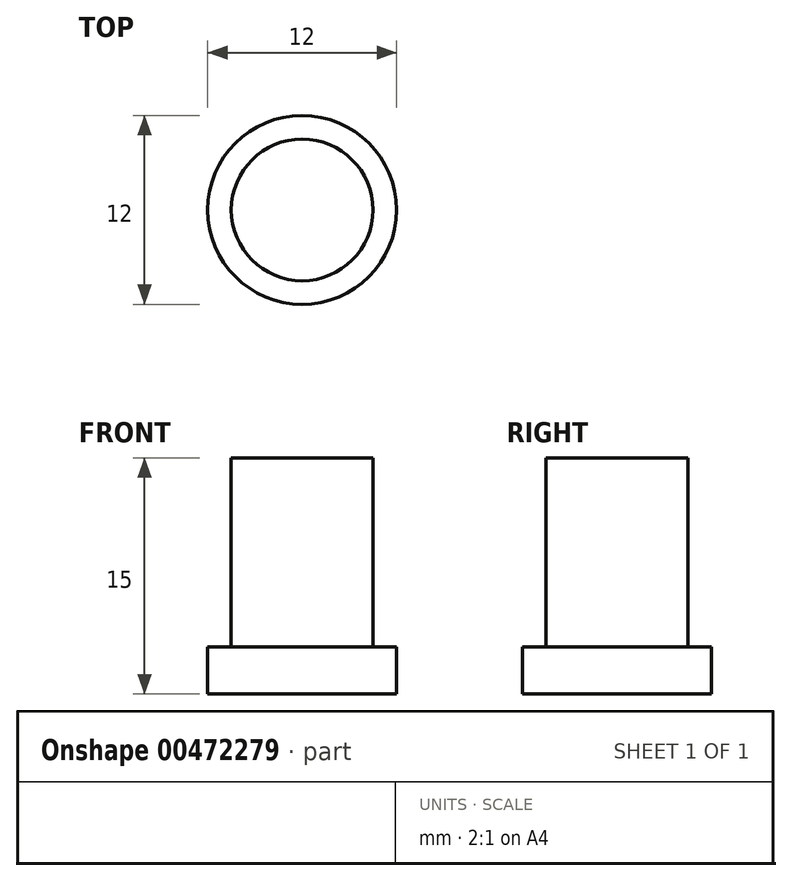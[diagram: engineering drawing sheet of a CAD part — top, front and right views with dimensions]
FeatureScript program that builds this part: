
annotation { "Feature Type Name" : "Feature", "Feature Type Description" : "" }
export const myFeature = defineFeature(function(context is Context, id is Id, definition is map)
    precondition{}
    {
        {
            var Q0;
            Q0=qCreatedBy(makeId("Top.planeOp"),FACE);
            var sketch = newSketch(context, id + "F0", { "sketchPlane" : qUnion([Q0])});
            skCircle(sketch, "E0", {"center": v(0, 0) * mm, "radius": 6 * mm});
            skCircle(sketch, "E1", {"center": v(0, 0) * mm, "radius": 4.5 * mm});
            skSolve(sketch);
        }
        {
            var Q0;
            Q0=makeQuery(id+"F0.imprint","IMPRINT",FACE,{"disambiguationData":[TD([[makeQuery(id+"F0.imprint","IMPRINT",EDGE,{"derivedFrom":sQuery(id+"F0.wireOp",EDGE,"E1")}),1.0]])]});
            extrude(context, id + "F1", {"entities" : qUnion([Q0]), "depth" : 12 * mm, "offsetDistance" : 25 * mm});
        }
        {
            var Q0;
            Q0 = qSketchRegion(id + "F0", true);
            var Q1;
            Q1=makeQuery(id+"F1.opExtrude","CAP_FACE",FACE,{"disambiguationData":[OSD([sQuery(id+"F0.wireOp",EDGE,"E1")])],"isStart":true});
            extrude(context, id + "F2", {"entities" : qUnion([Q0, Q1]), "operationType" : NewBodyOperationType.ADD, "oppositeDirection" : true, "depth" : 3 * mm, "offsetDistance" : 25 * mm});
        }
    });
